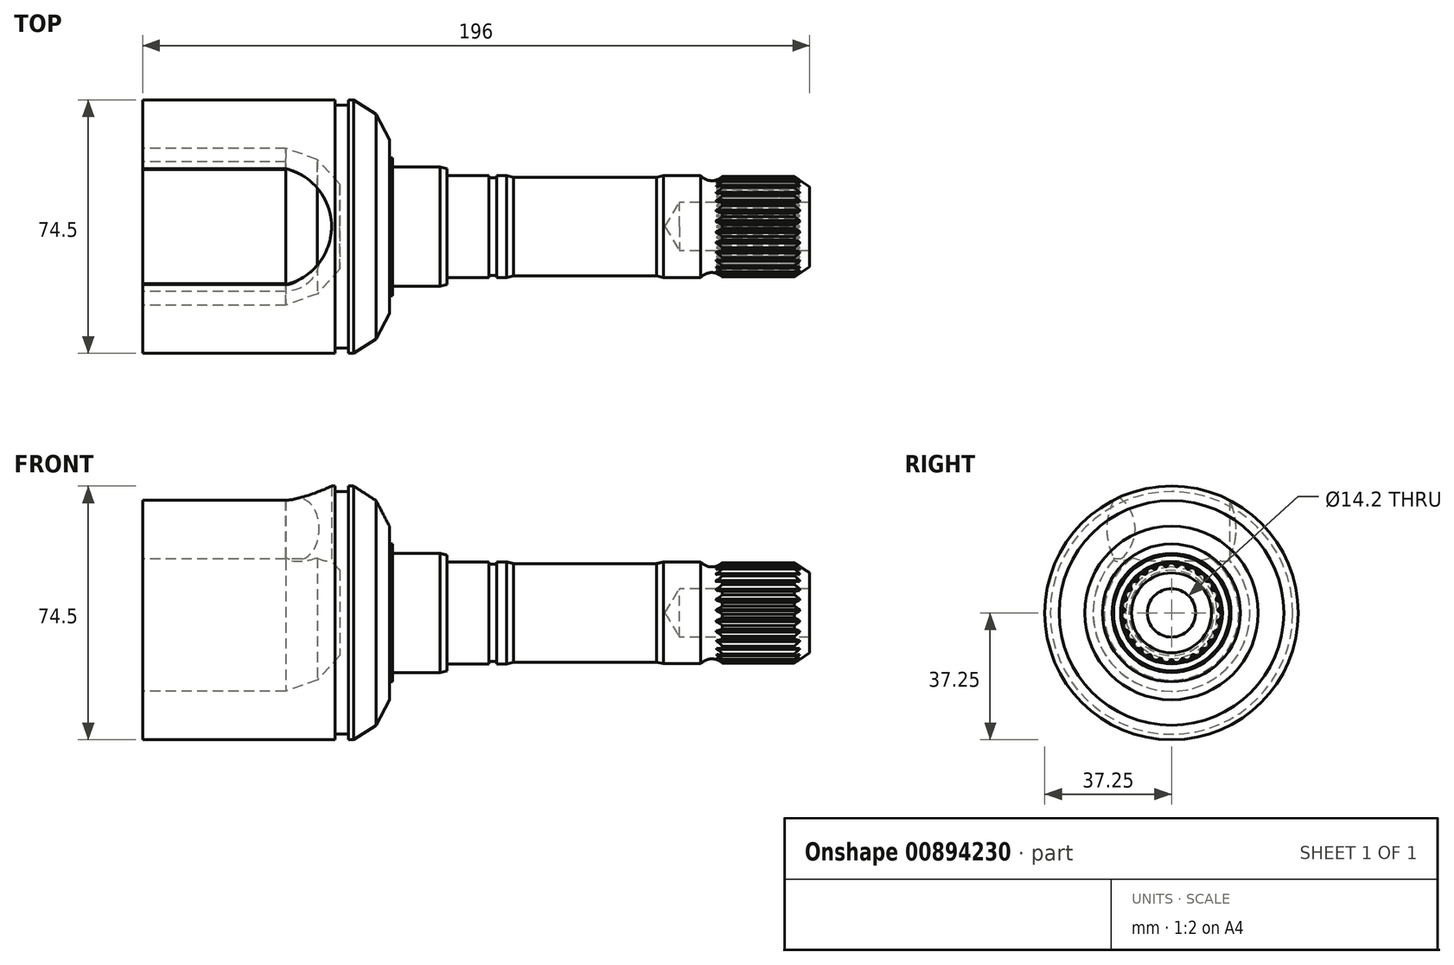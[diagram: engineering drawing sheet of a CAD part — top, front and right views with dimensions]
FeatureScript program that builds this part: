
annotation { "Feature Type Name" : "Feature", "Feature Type Description" : "" }
export const myFeature = defineFeature(function(context is Context, id is Id, definition is map)
    precondition{}
    {
        {
            var Q0;
            Q0=qCreatedBy(makeId("Front.planeOp"),FACE);
            var sketch = newSketch(context, id + "F0", { "sketchPlane" : qUnion([Q0])});
            skLineSegment(sketch, "E0", {"start": v(0, 37.25) * mm, "end": v(56.5, 37.25) * mm});
            skLineSegment(sketch, "E1", {"start": v(56.5, 37.25) * mm, "end": v(56.5, 35.65) * mm});
            skLineSegment(sketch, "E2", {"start": v(56.5, 35.65) * mm, "end": v(60.5, 35.65) * mm});
            skLineSegment(sketch, "E3", {"start": v(60.5, 35.65) * mm, "end": v(60.5, 37.25) * mm});
            skLineSegment(sketch, "E4", {"start": v(60.5, 37.25) * mm, "end": v(62, 37.25) * mm});
            skLineSegment(sketch, "E5", {"start": v(62, 37.25) * mm, "end": v(68.6, 33) * mm});
            skLineSegment(sketch, "E6", {"start": v(68.6, 33) * mm, "end": v(72.5, 25.5) * mm});
            skLineSegment(sketch, "E7", {"start": v(72.5, 25.5) * mm, "end": v(72.5, 20.25) * mm});
            skLineSegment(sketch, "E8", {"start": v(72.5, 20.25) * mm, "end": v(73.4, 20.25) * mm});
            skLineSegment(sketch, "E9", {"start": v(73.4, 20.25) * mm, "end": v(73.4, 17.5) * mm});
            skLineSegment(sketch, "E10", {"start": v(73.4, 17.5) * mm, "end": v(87.4, 17.5) * mm});
            skLineSegment(sketch, "E11", {"start": v(89.4, 17) * mm, "end": v(87.4, 17.5) * mm});
            skLineSegment(sketch, "E12", {"start": v(89.4, 17) * mm, "end": v(89.4, 15) * mm});
            skLineSegment(sketch, "E13", {"start": v(89.4, 15) * mm, "end": v(101.7, 15) * mm});
            skLineSegment(sketch, "E14", {"start": v(101.7, 15) * mm, "end": v(101.7, 14.3) * mm});
            skLineSegment(sketch, "E15", {"start": v(101.7, 14.3) * mm, "end": v(104, 14.3) * mm});
            skLineSegment(sketch, "E16", {"start": v(104, 14.3) * mm, "end": v(104, 15) * mm});
            skLineSegment(sketch, "E17", {"start": v(104, 15) * mm, "end": v(107, 15) * mm});
            skLineSegment(sketch, "E18", {"start": v(109, 14.5) * mm, "end": v(107, 15) * mm});
            skLineSegment(sketch, "E19", {"start": v(109, 14.5) * mm, "end": v(151, 14.5) * mm});
            skLineSegment(sketch, "E20", {"start": v(170.35, 14.75) * mm, "end": v(191.5, 14.75) * mm});
            skLineSegment(sketch, "E21", {"start": v(191.5, 14.75) * mm, "end": v(196, 11.75) * mm});
            skLineSegment(sketch, "E22", {"start": v(196, 11.75) * mm, "end": v(196, 7.1) * mm});
            skLineSegment(sketch, "E23", {"start": v(196, 7.1) * mm, "end": v(157.77, 7.1) * mm});
            skLineSegment(sketch, "E24", {"start": v(157.77, 7.1) * mm, "end": v(153.5, 0) * mm});
            skLineSegment(sketch, "E25", {"start": v(151, 14.5) * mm, "end": v(153, 14.95) * mm});
            skLineSegment(sketch, "E26", {"start": v(153, 14.95) * mm, "end": v(164, 14.95) * mm});
            skLineSegment(sketch, "E27", {"start": v(0, 37.25) * mm, "end": v(0, 23.05) * mm});
            skLineSegment(sketch, "E28", {"start": v(0, 23.05) * mm, "end": v(42, 23.05) * mm});
            skLineSegment(sketch, "E29", {"start": v(42, 23.05) * mm, "end": v(51.3, 19.75) * mm});
            skLineSegment(sketch, "E30", {"start": v(51.3, 19.75) * mm, "end": v(58, 12.5) * mm});
            skLineSegment(sketch, "E31", {"start": v(58, 12.5) * mm, "end": v(58, 0) * mm});
            skLineSegment(sketch, "E32", {"start": v(58, 0) * mm, "end": v(153.5, 0) * mm});
            skArc(sketch, "E33", {"start": v(164, 14.95) * mm, "mid": v(167.13, 13.5) * mm, "end": v(170.35, 14.75) * mm});
            skLineSegment(sketch, "E34", {"start": v(164.02, 13.5) * mm, "end": v(170.18, 13.5) * mm, "construction": true});
            skSolve(sketch);
        }
        {
            var Q0;
            Q0=makeQuery(id+"F0.imprint","IMPRINT",FACE,{"disambiguationData":[TD([[makeQuery(id+"F0.imprint","IMPRINT",EDGE,{"derivedFrom":sQuery(id+"F0.wireOp",EDGE,"E0")}),-1.0]])]});
            var Q1;
            Q1=sQuery(id+"F0.wireOp",EDGE,"E32");
            revolve(context, id + "F1", {"surfaceOperationType" : NewSurfaceOperationType.NEW, "entities" : qUnion([Q0]), "axis" : qUnion([Q1]), "revolveType" : RevolveType.FULL});
        }
        {
            var Q0;
            Q0=makeQuery(id+"F1.opRevolve","SWEPT_FACE",FACE,{"disambiguationData":[OSD([sQuery(id+"F0.wireOp",EDGE,"E22")])]});
            var sketch = newSketch(context, id + "F2", { "sketchPlane" : qUnion([Q0])});
            skArc(sketch, "E35", {"start": v(0.5, 14.72) * mm, "mid": v(0.25, 14.72) * mm, "end": v(0, 14.72) * mm});
            skArc(sketch, "E36", {"start": v(1.6, 13.58) * mm, "mid": v(1.5, 13.6) * mm, "end": v(1.4, 13.6) * mm});
            skLineSegment(sketch, "E37", {"start": v(1.4, 13.6) * mm, "end": v(0.5, 14.72) * mm});
            skArc(sketch, "E38", {"start": v(0, 14.72) * mm, "mid": v(-0.25, 14.72) * mm, "end": v(-0.5, 14.72) * mm});
            skArc(sketch, "E39", {"start": v(-1.4, 13.6) * mm, "mid": v(-1.5, 13.6) * mm, "end": v(-1.6, 13.58) * mm});
            skLineSegment(sketch, "E40", {"start": v(-1.4, 13.6) * mm, "end": v(-0.5, 14.72) * mm});
            skArc(sketch, "E41", {"start": v(-2.91, 14.43) * mm, "mid": v(-3.16, 14.38) * mm, "end": v(-3.4, 14.33) * mm});
            skArc(sketch, "E42", {"start": v(-1.6, 13.58) * mm, "mid": v(-1.69, 13.57) * mm, "end": v(-1.79, 13.56) * mm});
            skLineSegment(sketch, "E43", {"start": v(-1.79, 13.56) * mm, "end": v(-2.91, 14.43) * mm});
            skArc(sketch, "E44", {"start": v(-3.4, 14.33) * mm, "mid": v(-3.64, 14.27) * mm, "end": v(-3.89, 14.2) * mm});
            skArc(sketch, "E45", {"start": v(-4.5, 12.92) * mm, "mid": v(-4.6, 12.88) * mm, "end": v(-4.69, 12.85) * mm});
            skLineSegment(sketch, "E46", {"start": v(-4.5, 12.92) * mm, "end": v(-3.89, 14.2) * mm});
            skArc(sketch, "E47", {"start": v(-6.17, 13.37) * mm, "mid": v(-6.4, 13.27) * mm, "end": v(-6.62, 13.16) * mm});
            skArc(sketch, "E48", {"start": v(-4.69, 12.85) * mm, "mid": v(-4.78, 12.81) * mm, "end": v(-4.87, 12.78) * mm});
            skLineSegment(sketch, "E49", {"start": v(-4.87, 12.78) * mm, "end": v(-6.17, 13.37) * mm});
            skArc(sketch, "E50", {"start": v(-6.62, 13.16) * mm, "mid": v(-6.84, 13.04) * mm, "end": v(-7.06, 12.92) * mm});
            skArc(sketch, "E51", {"start": v(-7.36, 11.53) * mm, "mid": v(-7.44, 11.48) * mm, "end": v(-7.53, 11.42) * mm});
            skLineSegment(sketch, "E52", {"start": v(-7.36, 11.53) * mm, "end": v(-7.06, 12.92) * mm});
            skArc(sketch, "E53", {"start": v(-9.1, 11.59) * mm, "mid": v(-9.29, 11.43) * mm, "end": v(-9.48, 11.27) * mm});
            skArc(sketch, "E54", {"start": v(-7.53, 11.42) * mm, "mid": v(-7.61, 11.37) * mm, "end": v(-7.7, 11.31) * mm});
            skLineSegment(sketch, "E55", {"start": v(-7.7, 11.31) * mm, "end": v(-9.1, 11.59) * mm});
            skArc(sketch, "E56", {"start": v(-9.48, 11.27) * mm, "mid": v(-9.67, 11.11) * mm, "end": v(-9.86, 10.95) * mm});
            skArc(sketch, "E57", {"start": v(-9.83, 9.52) * mm, "mid": v(-9.9, 9.45) * mm, "end": v(-9.97, 9.38) * mm});
            skLineSegment(sketch, "E58", {"start": v(-9.83, 9.52) * mm, "end": v(-9.86, 10.95) * mm});
            skArc(sketch, "E59", {"start": v(-11.53, 9.18) * mm, "mid": v(-11.68, 8.98) * mm, "end": v(-11.83, 8.78) * mm});
            skArc(sketch, "E60", {"start": v(-9.97, 9.38) * mm, "mid": v(-10.03, 9.3) * mm, "end": v(-10.1, 9.23) * mm});
            skLineSegment(sketch, "E61", {"start": v(-10.1, 9.23) * mm, "end": v(-11.53, 9.18) * mm});
            skArc(sketch, "E62", {"start": v(-11.83, 8.78) * mm, "mid": v(-11.98, 8.58) * mm, "end": v(-12.12, 8.38) * mm});
            skArc(sketch, "E63", {"start": v(-11.76, 7) * mm, "mid": v(-11.81, 6.91) * mm, "end": v(-11.86, 6.82) * mm});
            skLineSegment(sketch, "E64", {"start": v(-11.76, 7) * mm, "end": v(-12.12, 8.38) * mm});
            skArc(sketch, "E65", {"start": v(-13.34, 6.27) * mm, "mid": v(-13.44, 6.05) * mm, "end": v(-13.54, 5.82) * mm});
            skArc(sketch, "E66", {"start": v(-11.86, 6.82) * mm, "mid": v(-11.91, 6.74) * mm, "end": v(-11.96, 6.65) * mm});
            skLineSegment(sketch, "E67", {"start": v(-11.96, 6.65) * mm, "end": v(-13.34, 6.27) * mm});
            skArc(sketch, "E68", {"start": v(-13.54, 5.82) * mm, "mid": v(-13.64, 5.59) * mm, "end": v(-13.73, 5.35) * mm});
            skArc(sketch, "E69", {"start": v(-13.07, 4.1) * mm, "mid": v(-13.1, 4) * mm, "end": v(-13.12, 3.9) * mm});
            skLineSegment(sketch, "E70", {"start": v(-13.07, 4.1) * mm, "end": v(-13.73, 5.35) * mm});
            skArc(sketch, "E71", {"start": v(-14.43, 3.03) * mm, "mid": v(-14.48, 2.78) * mm, "end": v(-14.53, 2.54) * mm});
            skArc(sketch, "E72", {"start": v(-13.12, 3.9) * mm, "mid": v(-13.15, 3.8) * mm, "end": v(-13.18, 3.71) * mm});
            skLineSegment(sketch, "E73", {"start": v(-13.18, 3.71) * mm, "end": v(-14.43, 3.03) * mm});
            skArc(sketch, "E74", {"start": v(-14.53, 2.54) * mm, "mid": v(-14.57, 2.29) * mm, "end": v(-14.6, 2.04) * mm});
            skArc(sketch, "E75", {"start": v(-13.66, 0.97) * mm, "mid": v(-13.67, 0.87) * mm, "end": v(-13.68, 0.77) * mm});
            skLineSegment(sketch, "E76", {"start": v(-13.66, 0.97) * mm, "end": v(-14.6, 2.04) * mm});
            skArc(sketch, "E77", {"start": v(-14.75, -0.38) * mm, "mid": v(-14.74, -0.63) * mm, "end": v(-14.73, -0.88) * mm});
            skArc(sketch, "E78", {"start": v(-13.68, 0.77) * mm, "mid": v(-13.68, 0.67) * mm, "end": v(-13.69, 0.57) * mm});
            skLineSegment(sketch, "E79", {"start": v(-13.69, 0.57) * mm, "end": v(-14.75, -0.38) * mm});
            skArc(sketch, "E80", {"start": v(-14.73, -0.88) * mm, "mid": v(-14.7, -1.13) * mm, "end": v(-14.69, -1.38) * mm});
            skArc(sketch, "E81", {"start": v(-13.53, -2.2) * mm, "mid": v(-13.5, -2.3) * mm, "end": v(-13.5, -2.4) * mm});
            skLineSegment(sketch, "E82", {"start": v(-13.53, -2.2) * mm, "end": v(-14.69, -1.38) * mm});
            skArc(sketch, "E83", {"start": v(-14.27, -3.77) * mm, "mid": v(-14.2, -4.02) * mm, "end": v(-14.13, -4.26) * mm});
            skArc(sketch, "E84", {"start": v(-13.5, -2.4) * mm, "mid": v(-13.47, -2.5) * mm, "end": v(-13.46, -2.6) * mm});
            skLineSegment(sketch, "E85", {"start": v(-13.46, -2.6) * mm, "end": v(-14.27, -3.77) * mm});
            skArc(sketch, "E86", {"start": v(-14.13, -4.26) * mm, "mid": v(-14.06, -4.5) * mm, "end": v(-13.98, -4.73) * mm});
            skArc(sketch, "E87", {"start": v(-12.66, -5.27) * mm, "mid": v(-12.62, -5.36) * mm, "end": v(-12.58, -5.45) * mm});
            skLineSegment(sketch, "E88", {"start": v(-12.66, -5.27) * mm, "end": v(-13.98, -4.73) * mm});
            skArc(sketch, "E89", {"start": v(-13.02, -6.96) * mm, "mid": v(-12.9, -7.18) * mm, "end": v(-12.77, -7.4) * mm});
            skArc(sketch, "E90", {"start": v(-12.58, -5.45) * mm, "mid": v(-12.54, -5.54) * mm, "end": v(-12.5, -5.63) * mm});
            skLineSegment(sketch, "E91", {"start": v(-12.5, -5.63) * mm, "end": v(-13.02, -6.96) * mm});
            skArc(sketch, "E92", {"start": v(-12.77, -7.4) * mm, "mid": v(-12.65, -7.62) * mm, "end": v(-12.52, -7.83) * mm});
            skArc(sketch, "E93", {"start": v(-11.1, -8.04) * mm, "mid": v(-11.05, -8.13) * mm, "end": v(-10.99, -8.2) * mm});
            skLineSegment(sketch, "E94", {"start": v(-11.1, -8.04) * mm, "end": v(-12.52, -7.83) * mm});
            skArc(sketch, "E95", {"start": v(-11.07, -9.78) * mm, "mid": v(-10.9, -9.96) * mm, "end": v(-10.73, -10.15) * mm});
            skArc(sketch, "E96", {"start": v(-10.99, -8.2) * mm, "mid": v(-10.93, -8.29) * mm, "end": v(-10.87, -8.37) * mm});
            skLineSegment(sketch, "E97", {"start": v(-10.87, -8.37) * mm, "end": v(-11.07, -9.78) * mm});
            skArc(sketch, "E98", {"start": v(-10.73, -10.15) * mm, "mid": v(-10.56, -10.33) * mm, "end": v(-10.38, -10.5) * mm});
            skArc(sketch, "E99", {"start": v(-8.96, -10.4) * mm, "mid": v(-8.88, -10.46) * mm, "end": v(-8.8, -10.52) * mm});
            skLineSegment(sketch, "E100", {"start": v(-8.96, -10.4) * mm, "end": v(-10.38, -10.5) * mm});
            skArc(sketch, "E101", {"start": v(-8.52, -12.07) * mm, "mid": v(-8.31, -12.2) * mm, "end": v(-8.1, -12.35) * mm});
            skArc(sketch, "E102", {"start": v(-8.8, -10.52) * mm, "mid": v(-8.73, -10.58) * mm, "end": v(-8.65, -10.65) * mm});
            skLineSegment(sketch, "E103", {"start": v(-8.65, -10.65) * mm, "end": v(-8.52, -12.07) * mm});
            skArc(sketch, "E104", {"start": v(-8.1, -12.35) * mm, "mid": v(-7.9, -12.48) * mm, "end": v(-7.68, -12.62) * mm});
            skArc(sketch, "E105", {"start": v(-6.33, -12.18) * mm, "mid": v(-6.24, -12.22) * mm, "end": v(-6.15, -12.27) * mm});
            skLineSegment(sketch, "E106", {"start": v(-6.33, -12.18) * mm, "end": v(-7.68, -12.62) * mm});
            skArc(sketch, "E107", {"start": v(-5.51, -13.7) * mm, "mid": v(-5.28, -13.8) * mm, "end": v(-5.04, -13.89) * mm});
            skArc(sketch, "E108", {"start": v(-6.15, -12.27) * mm, "mid": v(-6.06, -12.31) * mm, "end": v(-5.97, -12.36) * mm});
            skLineSegment(sketch, "E109", {"start": v(-5.97, -12.36) * mm, "end": v(-5.51, -13.7) * mm});
            skArc(sketch, "E110", {"start": v(-5.04, -13.89) * mm, "mid": v(-4.8, -13.97) * mm, "end": v(-4.57, -14.05) * mm});
            skArc(sketch, "E111", {"start": v(-3.35, -13.3) * mm, "mid": v(-3.26, -13.33) * mm, "end": v(-3.16, -13.36) * mm});
            skLineSegment(sketch, "E112", {"start": v(-3.35, -13.3) * mm, "end": v(-4.57, -14.05) * mm});
            skArc(sketch, "E113", {"start": v(-2.2, -14.6) * mm, "mid": v(-1.96, -14.64) * mm, "end": v(-1.71, -14.68) * mm});
            skArc(sketch, "E114", {"start": v(-3.16, -13.36) * mm, "mid": v(-3.06, -13.38) * mm, "end": v(-2.96, -13.4) * mm});
            skLineSegment(sketch, "E115", {"start": v(-2.96, -13.4) * mm, "end": v(-2.2, -14.6) * mm});
            skArc(sketch, "E116", {"start": v(-1.71, -14.68) * mm, "mid": v(-1.46, -14.7) * mm, "end": v(-1.21, -14.72) * mm});
            skArc(sketch, "E117", {"start": v(-0.2, -13.72) * mm, "mid": v(-0.1, -13.72) * mm, "end": v(0, -13.73) * mm});
            skLineSegment(sketch, "E118", {"start": v(-0.2, -13.72) * mm, "end": v(-1.21, -14.72) * mm});
            skArc(sketch, "E119", {"start": v(1.21, -14.72) * mm, "mid": v(1.46, -14.7) * mm, "end": v(1.71, -14.68) * mm});
            skArc(sketch, "E120", {"start": v(0, -13.73) * mm, "mid": v(0.1, -13.72) * mm, "end": v(0.2, -13.72) * mm});
            skLineSegment(sketch, "E121", {"start": v(0.2, -13.72) * mm, "end": v(1.21, -14.72) * mm});
            skArc(sketch, "E122", {"start": v(1.71, -14.68) * mm, "mid": v(1.96, -14.64) * mm, "end": v(2.2, -14.6) * mm});
            skArc(sketch, "E123", {"start": v(2.96, -13.4) * mm, "mid": v(3.06, -13.38) * mm, "end": v(3.16, -13.36) * mm});
            skLineSegment(sketch, "E124", {"start": v(2.96, -13.4) * mm, "end": v(2.2, -14.6) * mm});
            skArc(sketch, "E125", {"start": v(4.57, -14.05) * mm, "mid": v(4.8, -13.97) * mm, "end": v(5.04, -13.89) * mm});
            skArc(sketch, "E126", {"start": v(3.16, -13.36) * mm, "mid": v(3.26, -13.33) * mm, "end": v(3.35, -13.3) * mm});
            skLineSegment(sketch, "E127", {"start": v(3.35, -13.3) * mm, "end": v(4.57, -14.05) * mm});
            skArc(sketch, "E128", {"start": v(5.04, -13.89) * mm, "mid": v(5.28, -13.8) * mm, "end": v(5.51, -13.7) * mm});
            skArc(sketch, "E129", {"start": v(5.97, -12.36) * mm, "mid": v(6.06, -12.31) * mm, "end": v(6.15, -12.27) * mm});
            skLineSegment(sketch, "E130", {"start": v(5.97, -12.36) * mm, "end": v(5.51, -13.7) * mm});
            skArc(sketch, "E131", {"start": v(7.68, -12.62) * mm, "mid": v(7.9, -12.48) * mm, "end": v(8.1, -12.35) * mm});
            skArc(sketch, "E132", {"start": v(6.15, -12.27) * mm, "mid": v(6.24, -12.22) * mm, "end": v(6.33, -12.18) * mm});
            skLineSegment(sketch, "E133", {"start": v(6.33, -12.18) * mm, "end": v(7.68, -12.62) * mm});
            skArc(sketch, "E134", {"start": v(8.1, -12.35) * mm, "mid": v(8.31, -12.2) * mm, "end": v(8.52, -12.07) * mm});
            skArc(sketch, "E135", {"start": v(8.65, -10.65) * mm, "mid": v(8.73, -10.58) * mm, "end": v(8.8, -10.52) * mm});
            skLineSegment(sketch, "E136", {"start": v(8.65, -10.65) * mm, "end": v(8.52, -12.07) * mm});
            skArc(sketch, "E137", {"start": v(10.38, -10.5) * mm, "mid": v(10.56, -10.33) * mm, "end": v(10.73, -10.15) * mm});
            skArc(sketch, "E138", {"start": v(8.8, -10.52) * mm, "mid": v(8.88, -10.46) * mm, "end": v(8.96, -10.4) * mm});
            skLineSegment(sketch, "E139", {"start": v(8.96, -10.4) * mm, "end": v(10.38, -10.5) * mm});
            skArc(sketch, "E140", {"start": v(10.73, -10.15) * mm, "mid": v(10.9, -9.96) * mm, "end": v(11.07, -9.78) * mm});
            skArc(sketch, "E141", {"start": v(10.87, -8.37) * mm, "mid": v(10.93, -8.29) * mm, "end": v(10.99, -8.2) * mm});
            skLineSegment(sketch, "E142", {"start": v(10.87, -8.37) * mm, "end": v(11.07, -9.78) * mm});
            skArc(sketch, "E143", {"start": v(12.52, -7.83) * mm, "mid": v(12.65, -7.62) * mm, "end": v(12.77, -7.4) * mm});
            skArc(sketch, "E144", {"start": v(10.99, -8.2) * mm, "mid": v(11.05, -8.13) * mm, "end": v(11.1, -8.04) * mm});
            skLineSegment(sketch, "E145", {"start": v(11.1, -8.04) * mm, "end": v(12.52, -7.83) * mm});
            skArc(sketch, "E146", {"start": v(12.77, -7.4) * mm, "mid": v(12.9, -7.18) * mm, "end": v(13.02, -6.96) * mm});
            skArc(sketch, "E147", {"start": v(12.5, -5.63) * mm, "mid": v(12.54, -5.54) * mm, "end": v(12.58, -5.45) * mm});
            skLineSegment(sketch, "E148", {"start": v(12.5, -5.63) * mm, "end": v(13.02, -6.96) * mm});
            skArc(sketch, "E149", {"start": v(13.98, -4.73) * mm, "mid": v(14.06, -4.5) * mm, "end": v(14.13, -4.26) * mm});
            skArc(sketch, "E150", {"start": v(12.58, -5.45) * mm, "mid": v(12.62, -5.36) * mm, "end": v(12.66, -5.27) * mm});
            skLineSegment(sketch, "E151", {"start": v(12.66, -5.27) * mm, "end": v(13.98, -4.73) * mm});
            skArc(sketch, "E152", {"start": v(14.13, -4.26) * mm, "mid": v(14.2, -4.02) * mm, "end": v(14.27, -3.77) * mm});
            skArc(sketch, "E153", {"start": v(13.46, -2.6) * mm, "mid": v(13.47, -2.5) * mm, "end": v(13.5, -2.4) * mm});
            skLineSegment(sketch, "E154", {"start": v(13.46, -2.6) * mm, "end": v(14.27, -3.77) * mm});
            skArc(sketch, "E155", {"start": v(14.69, -1.38) * mm, "mid": v(14.7, -1.13) * mm, "end": v(14.73, -0.88) * mm});
            skArc(sketch, "E156", {"start": v(13.5, -2.4) * mm, "mid": v(13.5, -2.3) * mm, "end": v(13.53, -2.2) * mm});
            skLineSegment(sketch, "E157", {"start": v(13.53, -2.2) * mm, "end": v(14.69, -1.38) * mm});
            skArc(sketch, "E158", {"start": v(14.73, -0.88) * mm, "mid": v(14.74, -0.63) * mm, "end": v(14.75, -0.38) * mm});
            skArc(sketch, "E159", {"start": v(13.69, 0.57) * mm, "mid": v(13.68, 0.67) * mm, "end": v(13.68, 0.77) * mm});
            skLineSegment(sketch, "E160", {"start": v(13.69, 0.57) * mm, "end": v(14.75, -0.38) * mm});
            skArc(sketch, "E161", {"start": v(14.6, 2.04) * mm, "mid": v(14.57, 2.29) * mm, "end": v(14.53, 2.54) * mm});
            skArc(sketch, "E162", {"start": v(13.68, 0.77) * mm, "mid": v(13.67, 0.87) * mm, "end": v(13.66, 0.97) * mm});
            skLineSegment(sketch, "E163", {"start": v(13.66, 0.97) * mm, "end": v(14.6, 2.04) * mm});
            skArc(sketch, "E164", {"start": v(14.53, 2.54) * mm, "mid": v(14.48, 2.78) * mm, "end": v(14.43, 3.03) * mm});
            skArc(sketch, "E165", {"start": v(13.18, 3.71) * mm, "mid": v(13.15, 3.8) * mm, "end": v(13.12, 3.9) * mm});
            skLineSegment(sketch, "E166", {"start": v(13.18, 3.71) * mm, "end": v(14.43, 3.03) * mm});
            skArc(sketch, "E167", {"start": v(13.73, 5.35) * mm, "mid": v(13.64, 5.59) * mm, "end": v(13.54, 5.82) * mm});
            skArc(sketch, "E168", {"start": v(13.12, 3.9) * mm, "mid": v(13.1, 4) * mm, "end": v(13.07, 4.1) * mm});
            skLineSegment(sketch, "E169", {"start": v(13.07, 4.1) * mm, "end": v(13.73, 5.35) * mm});
            skArc(sketch, "E170", {"start": v(13.54, 5.82) * mm, "mid": v(13.44, 6.05) * mm, "end": v(13.34, 6.27) * mm});
            skArc(sketch, "E171", {"start": v(11.96, 6.65) * mm, "mid": v(11.91, 6.74) * mm, "end": v(11.86, 6.82) * mm});
            skLineSegment(sketch, "E172", {"start": v(11.96, 6.65) * mm, "end": v(13.34, 6.27) * mm});
            skArc(sketch, "E173", {"start": v(12.12, 8.38) * mm, "mid": v(11.98, 8.58) * mm, "end": v(11.83, 8.78) * mm});
            skArc(sketch, "E174", {"start": v(11.86, 6.82) * mm, "mid": v(11.81, 6.91) * mm, "end": v(11.76, 7) * mm});
            skLineSegment(sketch, "E175", {"start": v(11.76, 7) * mm, "end": v(12.12, 8.38) * mm});
            skArc(sketch, "E176", {"start": v(11.83, 8.78) * mm, "mid": v(11.68, 8.98) * mm, "end": v(11.53, 9.18) * mm});
            skArc(sketch, "E177", {"start": v(10.1, 9.23) * mm, "mid": v(10.03, 9.3) * mm, "end": v(9.97, 9.38) * mm});
            skLineSegment(sketch, "E178", {"start": v(10.1, 9.23) * mm, "end": v(11.53, 9.18) * mm});
            skArc(sketch, "E179", {"start": v(9.86, 10.95) * mm, "mid": v(9.67, 11.11) * mm, "end": v(9.48, 11.27) * mm});
            skArc(sketch, "E180", {"start": v(9.97, 9.38) * mm, "mid": v(9.9, 9.45) * mm, "end": v(9.83, 9.52) * mm});
            skLineSegment(sketch, "E181", {"start": v(9.83, 9.52) * mm, "end": v(9.86, 10.95) * mm});
            skArc(sketch, "E182", {"start": v(9.48, 11.27) * mm, "mid": v(9.29, 11.43) * mm, "end": v(9.1, 11.59) * mm});
            skArc(sketch, "E183", {"start": v(7.7, 11.31) * mm, "mid": v(7.61, 11.37) * mm, "end": v(7.53, 11.42) * mm});
            skLineSegment(sketch, "E184", {"start": v(7.7, 11.31) * mm, "end": v(9.1, 11.59) * mm});
            skArc(sketch, "E185", {"start": v(7.06, 12.92) * mm, "mid": v(6.84, 13.04) * mm, "end": v(6.62, 13.16) * mm});
            skArc(sketch, "E186", {"start": v(7.53, 11.42) * mm, "mid": v(7.44, 11.48) * mm, "end": v(7.36, 11.53) * mm});
            skLineSegment(sketch, "E187", {"start": v(7.36, 11.53) * mm, "end": v(7.06, 12.92) * mm});
            skArc(sketch, "E188", {"start": v(6.62, 13.16) * mm, "mid": v(6.4, 13.27) * mm, "end": v(6.17, 13.37) * mm});
            skArc(sketch, "E189", {"start": v(4.87, 12.78) * mm, "mid": v(4.78, 12.81) * mm, "end": v(4.69, 12.85) * mm});
            skLineSegment(sketch, "E190", {"start": v(4.87, 12.78) * mm, "end": v(6.17, 13.37) * mm});
            skArc(sketch, "E191", {"start": v(3.89, 14.2) * mm, "mid": v(3.64, 14.27) * mm, "end": v(3.4, 14.33) * mm});
            skArc(sketch, "E192", {"start": v(4.69, 12.85) * mm, "mid": v(4.6, 12.88) * mm, "end": v(4.5, 12.92) * mm});
            skLineSegment(sketch, "E193", {"start": v(4.5, 12.92) * mm, "end": v(3.89, 14.2) * mm});
            skArc(sketch, "E194", {"start": v(3.4, 14.33) * mm, "mid": v(3.16, 14.38) * mm, "end": v(2.91, 14.43) * mm});
            skArc(sketch, "E195", {"start": v(1.79, 13.56) * mm, "mid": v(1.69, 13.57) * mm, "end": v(1.6, 13.58) * mm});
            skLineSegment(sketch, "E196", {"start": v(1.79, 13.56) * mm, "end": v(2.91, 14.43) * mm});
            skCircle(sketch, "E197", {"center": v(0, 0) * mm, "radius": 15.61 * mm});
            skSolve(sketch);
        }
        {
            var Q0;
            Q0=makeQuery(id+"F2.imprint","IMPRINT",FACE,{"disambiguationData":[TD([[makeQuery(id+"F2.imprint","IMPRINT",EDGE,{"derivedFrom":sQuery(id+"F2.wireOp",EDGE,"E35")}),-1.0]])]});
            extrude(context, id + "F3", {"entities" : qUnion([Q0]), "operationType" : NewBodyOperationType.REMOVE, "oppositeDirection" : true, "depth" : 28 * mm, "offsetDistance" : 25 * mm});
        }
        {
            var Q0;
            Q0=qCreatedBy(makeId("Right.planeOp"),FACE);
            var sketch = newSketch(context, id + "F4", { "sketchPlane" : qUnion([Q0])});
            skArc(sketch, "E198", {"start": v(17.03, 33.13) * mm, "mid": v(0, 37.25) * mm, "end": v(-17.03, 33.13) * mm});
            skArc(sketch, "E199", {"start": v(-17.03, 33.13) * mm, "mid": v(-19, 24.43) * mm, "end": v(-16.79, 15.8) * mm});
            skArc(sketch, "E200", {"start": v(16.79, 15.8) * mm, "mid": v(19, 24.43) * mm, "end": v(17.03, 33.13) * mm});
            skLineSegment(sketch, "E201", {"start": v(16.79, 15.8) * mm, "end": v(0, 0) * mm});
            skLineSegment(sketch, "E202", {"start": v(-16.79, 15.8) * mm, "end": v(0, 0) * mm});
            skSolve(sketch);
        }
        {
            var Q0;
            Q0=makeQuery(id+"F4.imprint","IMPRINT",FACE,{"disambiguationData":[TD([[makeQuery(id+"F4.imprint","IMPRINT",EDGE,{"derivedFrom":sQuery(id+"F4.wireOp",EDGE,"E198")}),1.0]])]});
            extrude(context, id + "F5", {"entities" : qUnion([Q0]), "operationType" : NewBodyOperationType.REMOVE, "depth" : 42 * mm, "offsetDistance" : 25 * mm, "hasDraft" : true, "draftAngle" : 0 * degree});
        }
        {
            var Q0;
            Q0=qCreatedBy(makeId("Top.planeOp"),FACE);
            var sketch = newSketch(context, id + "F6", { "sketchPlane" : qUnion([Q0])});
            skLineSegment(sketch, "E203", {"start": v(0, 0) * mm, "end": v(55.5, 0) * mm, "construction": true});
            skLineSegment(sketch, "E204", {"start": v(42, 17.03) * mm, "end": v(42, -17.03) * mm});
            skArc(sketch, "E205", {"start": v(42, -17.03) * mm, "mid": v(55.5, 0) * mm, "end": v(42, 17.03) * mm});
            skSolve(sketch);
        }
        {
            var Q0;
            Q0=makeQuery(id+"F6.imprint","IMPRINT",FACE,{"disambiguationData":[TD([[makeQuery(id+"F6.imprint","IMPRINT",EDGE,{"derivedFrom":sQuery(id+"F6.wireOp",EDGE,"E204")}),1.0]])]});
            extrude(context, id + "F7", {"entities" : qUnion([Q0]), "operationType" : NewBodyOperationType.REMOVE, "depth" : 37.25 * mm, "offsetDistance" : 25 * mm});
        }
        {
            var Q0;
            {var subQ0=sQuery(id+"F4.wireOp",EDGE,"E200");Q0=makeQuery(id+"F7.boolean.opBoolean","COPY",FACE,{"disambiguationData":[TD([makeQuery(id+"F5.boolean.opBoolean","COPY",FACE,{"derivedFrom":makeQuery(id+"F5.opExtrude","SWEPT_FACE",FACE,{"disambiguationData":[OSD([subQ0])]})})])],"derivedFrom":makeQuery(id+"F7.opExtrude","SWEPT_FACE",FACE,{"disambiguationData":[OSD([sQuery(id+"F6.wireOp",EDGE,"E204")])]})});}
            var sketch = newSketch(context, id + "F8", { "sketchPlane" : qUnion([Q0])});
            skLineSegment(sketch, "E206", {"start": v(-9, 28.9) * mm, "end": v(-9, 20.5) * mm, "construction": true});
            skLineSegment(sketch, "E207", {"start": v(-13, 34) * mm, "end": v(-13, 15.8) * mm});
            skLineSegment(sketch, "E208", {"start": v(-16.57, 34) * mm, "end": v(-13, 34) * mm});
            skLineSegment(sketch, "E209", {"start": v(-13, 15.8) * mm, "end": v(-16.79, 15.8) * mm});
            skArc(sketch, "E210", {"start": v(-16.57, 34) * mm, "mid": v(-19, 24.93) * mm, "end": v(-16.79, 15.8) * mm});
            skSolve(sketch);
        }
        {
            var Q0;
            Q0=qSketchRegion(id+"F8",true);
            var Q1;
            Q1=sQuery(id+"F8.wireOp",EDGE,"E206");
            revolve(context, id + "F9", {"operationType" : NewBodyOperationType.REMOVE, "surfaceOperationType" : NewSurfaceOperationType.NEW, "entities" : qUnion([Q0]), "axis" : qUnion([Q1]), "revolveType" : RevolveType.ONE_DIRECTION, "oppositeDirection" : true, "angle" : 82 * degree});
        }
    });
